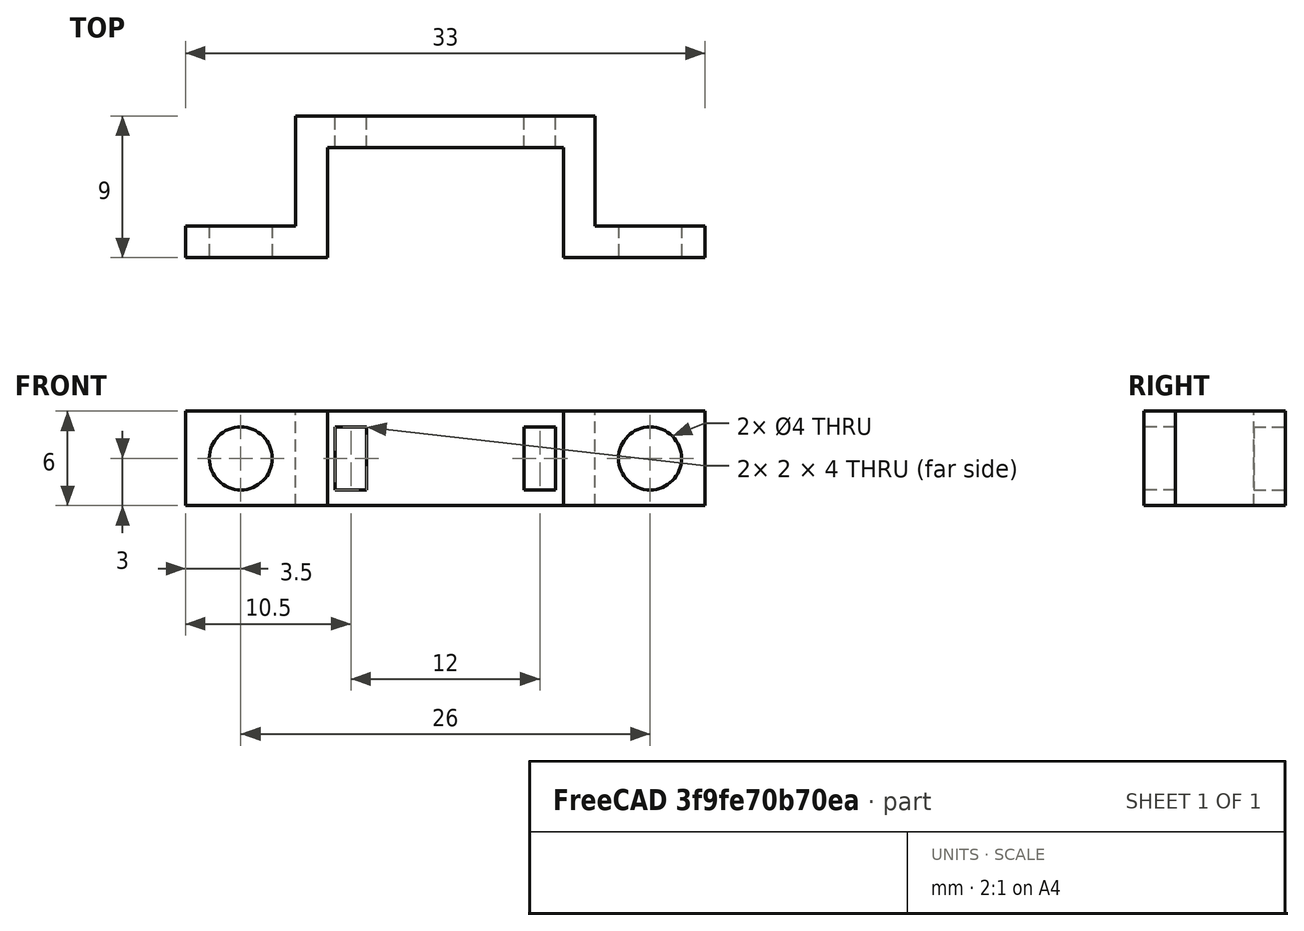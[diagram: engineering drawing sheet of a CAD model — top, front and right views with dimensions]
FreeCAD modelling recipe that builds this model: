
FCSTD DOCUMENT  (FreeCAD 0.18R16161 (Git))
Label: potSupport
License: All rights reserved
LicenseURL: http://en.wikipedia.org/wiki/All_rights_reserved
objects: Part::Box×7, Part::Cut×4, Part::MultiFuse×4, Part::Cylinder×2
note: 17 computed .brp shape members not serialized (recipe doc carries the construction recipe); baked Part::Feature solids carry a one-line shape summary decoded from their .brp

FEATURE [Part::Box] Box  label="Cube"
  AttacherType = Attacher::AttachEngine3D
  Height = 6
  Length = 19
  Width = 2
FEATURE [Part::Box] Box001  label="Cube001"
  AttacherType = Attacher::AttachEngine3D
  Height = 6
  Length = 2
  Placement = pos=(0,-7,0) rot=(0,0,1;0rad)
  Width = 7
FEATURE [Part::Box] Box002  label="Cube002"
  AttacherType = Attacher::AttachEngine3D
  Height = 6
  Length = 2
  Placement = pos=(17,-7,0) rot=(0,0,1;0rad)
  Width = 7
FEATURE [Part::Box] Box003  label="Cube003"
  AttacherType = Attacher::AttachEngine3D
  Height = 6
  Length = 7
  Placement = pos=(-7,-7,0) rot=(0,0,1;0rad)
  Width = 2
FEATURE [Part::Box] Box004  label="Cube004"
  AttacherType = Attacher::AttachEngine3D
  Height = 6
  Length = 7
  Placement = pos=(19,-7,0) rot=(0,0,1;0rad)
  Width = 2
FEATURE [Part::Cylinder] Cylinder
  Angle = 360
  AttacherType = Attacher::AttachEngine3D
  Height = 10
  Placement = pos=(-3.5,0,3) rot=(1,0,0;1.5708rad)
  Radius = 2
FEATURE [Part::Cylinder] Cylinder001
  Angle = 360
  AttacherType = Attacher::AttachEngine3D
  Height = 10
  Placement = pos=(22.5,0,3) rot=(1,0,0;1.5708rad)
  Radius = 2
FEATURE [Part::Cut] Cut
  Base = -> Box003
  Tool = -> Cylinder
FEATURE [Part::Cut] Cut001
  Base = -> Box004
  Tool = -> Cylinder001
FEATURE [Part::Box] Box005  label="Cube005"
  AttacherType = Attacher::AttachEngine3D
  Height = 4
  Length = 2
  Placement = pos=(2.5,-3,1) rot=(0,0,1;0rad)
  Width = 6
FEATURE [Part::Box] Box006  label="Cube006"
  AttacherType = Attacher::AttachEngine3D
  Height = 4
  Length = 2
  Placement = pos=(14.5,-3,1) rot=(0,0,1;0rad)
  Width = 6
FEATURE [Part::Cut] Cut002
  Base = -> Box
  Tool = -> Box005
FEATURE [Part::Cut] Cut003
  Base = -> Cut002
  Tool = -> Box006
FEATURE [Part::MultiFuse] Fusion
  Shapes = -> [Cut,Box001]
FEATURE [Part::MultiFuse] Fusion001
  Shapes = -> [Cut003,Fusion]
FEATURE [Part::MultiFuse] Fusion002
  Shapes = -> [Fusion001,Box002]
FEATURE [Part::MultiFuse] Fusion003
  Shapes = -> [Fusion002,Cut001]
